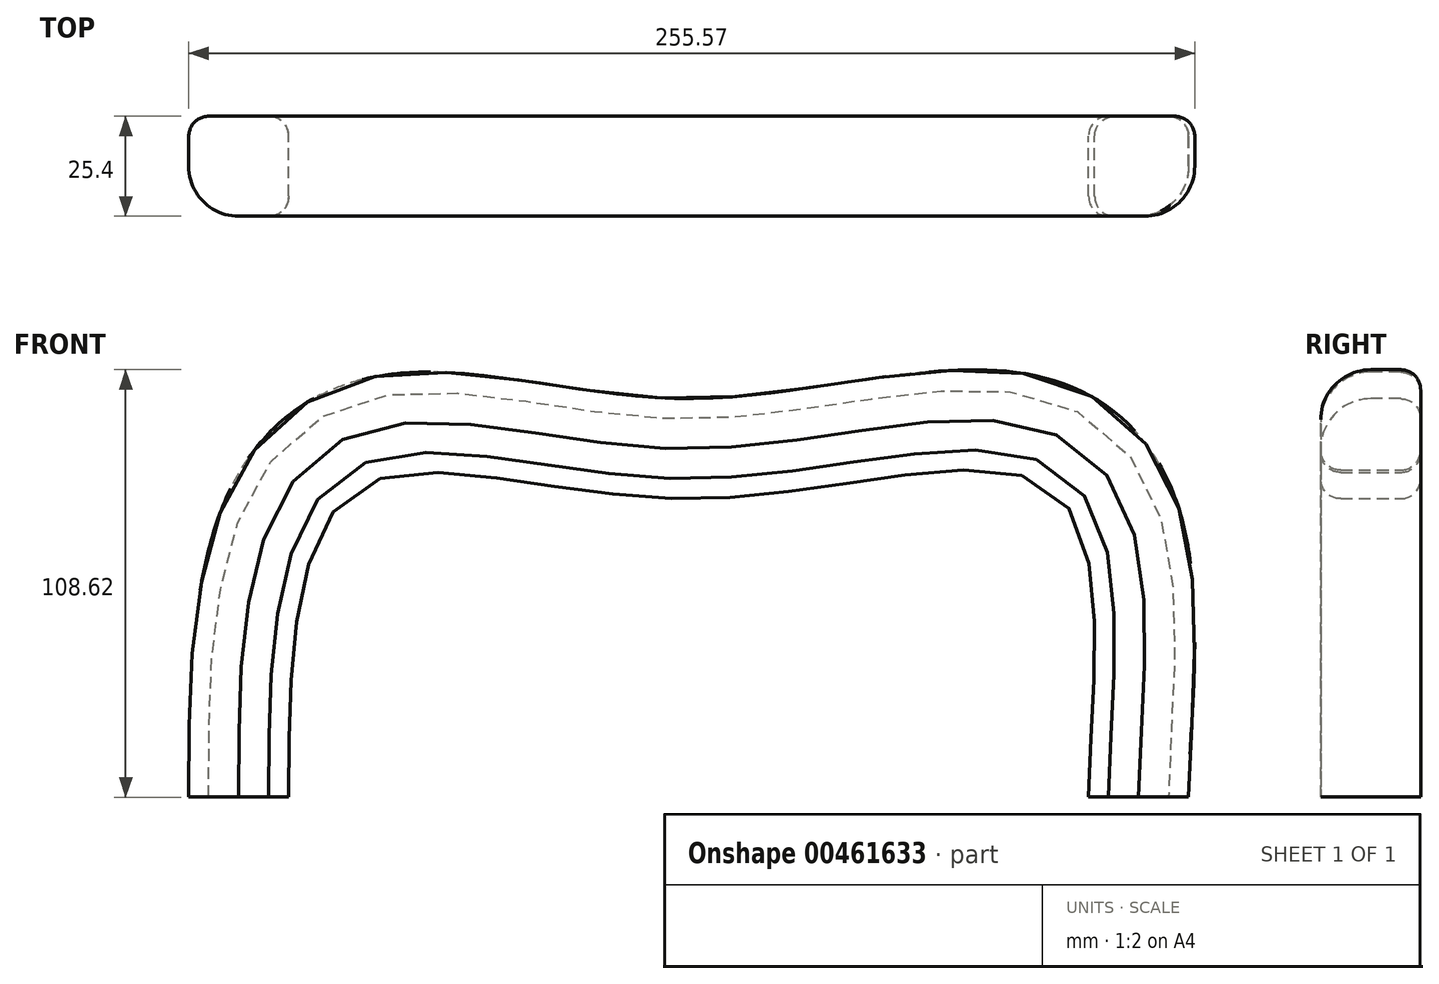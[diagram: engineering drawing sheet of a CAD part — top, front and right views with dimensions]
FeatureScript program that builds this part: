
annotation { "Feature Type Name" : "Feature", "Feature Type Description" : "" }
export const myFeature = defineFeature(function(context is Context, id is Id, definition is map)
    precondition{}
    {
        {
            var Q0;
            Q0=qCreatedBy(makeId("Front.planeOp"),FACE);
            var sketch = newSketch(context, id + "F0", { "sketchPlane" : qUnion([Q0])});
            skFitSpline(sketch, "E0", {"points": [v(-101.6, 0) * mm, v(-86.78, 76.36) * mm, v(0, 75.81) * mm, v(94.17, 76.36) * mm, v(101.6, 0) * mm], "startDerivative": vector(0, 295.5) * mm, "endDerivative": vector(0, -285.44) * mm});
            skLineSegment(sketch, "E1", {"start": v(-101.6, 0) * mm, "end": v(101.6, 0) * mm, "construction": true});
            skFitSpline(sketch, "E2.0", {"points": [v(-127, 0) * mm, v(-127, 3.03) * mm, v(-127.02, 9.8) * mm, v(-126.88, 21.44) * mm, v(-126.34, 34) * mm, v(-125.3, 44.86) * mm, v(-123.95, 53.64) * mm, v(-122.6, 60.25) * mm, v(-120.84, 66.87) * mm, v(-118.55, 73.5) * mm, v(-115.54, 80.13) * mm, v(-112.25, 85.62) * mm, v(-109.4, 89.37) * mm, v(-107.58, 91.47) * mm, v(-106.13, 93.01) * mm, v(-104.85, 94.27) * mm, v(-103.77, 95.24) * mm, v(-102.66, 96.2) * mm, v(-101.23, 97.35) * mm, v(-98.9, 99.06) * mm, v(-95.87, 100.95) * mm, v(-92.16, 102.84) * mm, v(-88.42, 104.37) * mm, v(-83.48, 105.95) * mm, v(-77.45, 107.2) * mm, v(-70.54, 107.87) * mm, v(-63.93, 107.95) * mm, v(-57.53, 107.62) * mm, v(-51.28, 107.02) * mm, v(-45.14, 106.25) * mm, v(-39.06, 105.37) * mm, v(-33.04, 104.46) * mm, v(-27.06, 103.56) * mm, v(-21.15, 102.75) * mm, v(-16.28, 102.17) * mm, v(-12.43, 101.8) * mm, v(-9.57, 101.57) * mm, v(-6.74, 101.39) * mm, v(-3.94, 101.27) * mm, v(-1.63, 101.22) * mm, v(0.19, 101.2) * mm, v(2.02, 101.22) * mm, v(4.36, 101.29) * mm, v(8.2, 101.47) * mm, v(13.12, 101.84) * mm, v(19.22, 102.48) * mm, v(25.46, 103.28) * mm, v(31.8, 104.18) * mm, v(38.2, 105.13) * mm, v(44.66, 106.08) * mm, v(51.15, 106.97) * mm, v(57.67, 107.73) * mm, v(64.25, 108.3) * mm, v(70.92, 108.57) * mm, v(77.74, 108.42) * mm, v(84.8, 107.7) * mm, v(90.96, 106.36) * mm, v(96.02, 104.68) * mm, v(99.85, 103.05) * mm, v(103.66, 101) * mm, v(106.77, 98.93) * mm, v(109.17, 97.04) * mm, v(110.62, 95.77) * mm, v(111.75, 94.7) * mm, v(112.85, 93.6) * mm, v(114.15, 92.2) * mm, v(115.6, 90.45) * mm, v(117.36, 88.1) * mm, v(119.29, 85.1) * mm, v(121.21, 81.5) * mm, v(123.33, 76.72) * mm, v(125.26, 70.82) * mm, v(126.79, 63.9) * mm, v(127.75, 57.13) * mm, v(128.3, 50.45) * mm, v(128.54, 43.87) * mm, v(128.54, 37.4) * mm, v(128.34, 28.98) * mm, v(127.93, 20.93) * mm, v(127.5, 13.53) * mm, v(127.23, 8.4) * mm, v(127.04, 3.8) * mm, v(127, 1.17) * mm, v(127, 0) * mm]});
            skLineSegment(sketch, "E3", {"start": v(-127, 0) * mm, "end": v(-101.6, 0) * mm});
            skLineSegment(sketch, "E4", {"start": v(101.6, 0) * mm, "end": v(127, 0) * mm});
            skSolve(sketch);
        }
        {
            var Q0;
            Q0 = qSketchRegion(id + "F0", true);
            extrude(context, id + "F1", {"entities" : qUnion([Q0]), "depth" : 25.4 * mm});
        }
        {
            var Q0;
            Q0=makeQuery(id+"F1.opExtrude","CAP_EDGE",EDGE,{"disambiguationData":[OSD([sQuery(id+"F0.wireOp",EDGE,"E2.0")])],"isStart":false});
            fillet(context, id + "F2", {"entities" : qUnion([Q0]), "radius" : 12.7 * mm, "tangentPropagation" : true, "allowEdgeOverflow" : false});
        }
        {
            var Q0;
            Q0=makeQuery(id+"F1.opExtrude","CAP_EDGE",EDGE,{"disambiguationData":[OSD([sQuery(id+"F0.wireOp",EDGE,"E0")])],"isStart":false});
            var Q1;
            Q1=makeQuery(id+"F1.opExtrude","CAP_EDGE",EDGE,{"disambiguationData":[OSD([sQuery(id+"F0.wireOp",EDGE,"E2.0")])],"isStart":true});
            var Q2;
            Q2=makeQuery(id+"F1.opExtrude","CAP_EDGE",EDGE,{"disambiguationData":[OSD([sQuery(id+"F0.wireOp",EDGE,"E0")])],"isStart":true});
            fillet(context, id + "F3", {"entities" : qUnion([Q0, Q1, Q2]), "radius" : 5.08 * mm, "tangentPropagation" : true, "allowEdgeOverflow" : false});
        }
    });
